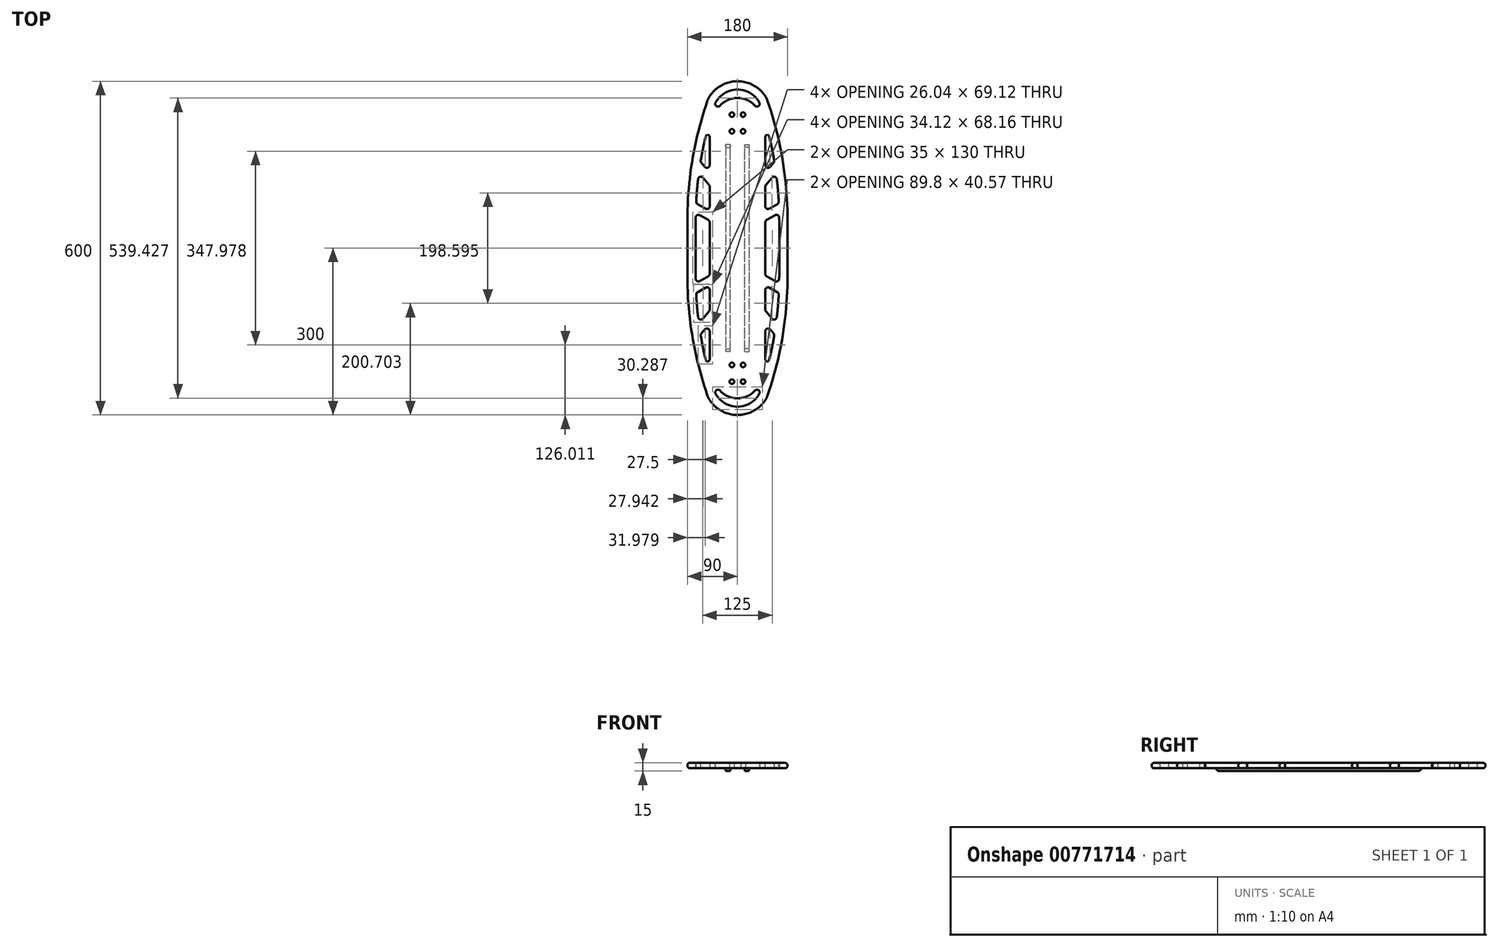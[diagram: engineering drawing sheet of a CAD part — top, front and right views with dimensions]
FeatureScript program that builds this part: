
annotation { "Feature Type Name" : "Feature", "Feature Type Description" : "" }
export const myFeature = defineFeature(function(context is Context, id is Id, definition is map)
    precondition{}
    {
        {
            var Q0;
            Q0=qCreatedBy(makeId("Top.planeOp"),FACE);
            var sketch = newSketch(context, id + "F0", { "sketchPlane" : qUnion([Q0])});
            skLineSegment(sketch, "E0", {"start": v(0, 0) * mm, "end": v(0, 270) * mm});
            skLineSegment(sketch, "E1", {"start": v(0, 0) * mm, "end": v(-50, 0) * mm});
            skLineSegment(sketch, "E2", {"start": v(-90, 0) * mm, "end": v(-90, 50) * mm});
            skArc(sketch, "E3", {"start": v(-53.96, 265.12) * mm, "mid": v(-80.93, 159.06) * mm, "end": v(-90, 50) * mm});
            skPoint(sketch, "E3.first.point", {"position": v(-90, 50) * mm});
            skArc(sketch, "E4", {"start": v(0, 300) * mm, "mid": v(-28.24, 292.94) * mm, "end": v(-49.83, 273.42) * mm});
            skPoint(sketch, "E5.visualSharp", {"position": v(-52.75, 268.59) * mm});
            skArc(sketch, "E5.filletArc", {"start": v(-49.83, 273.42) * mm, "mid": v(-52.16, 269.4) * mm, "end": v(-53.96, 265.12) * mm});
            skLineSegment(sketch, "E6", {"start": v(-75, 0) * mm, "end": v(-75, 50) * mm});
            skLineSegment(sketch, "E7", {"start": v(-50, 200) * mm, "end": v(-50, 149.42) * mm});
            skLineSegment(sketch, "E8.trimOffspring", {"start": v(-75, 0) * mm, "end": v(-90, 0) * mm});
            skPoint(sketch, "E9.visualSharp", {"position": v(-50, 27.86) * mm});
            skArc(sketch, "E10", {"start": v(-57.11, 200.84) * mm, "mid": v(-61.92, 179.23) * mm, "end": v(-65.98, 157.47) * mm});
            skArc(sketch, "E11", {"start": v(-50, 200) * mm, "mid": v(-53.18, 203.58) * mm, "end": v(-57.11, 200.84) * mm});
            skPoint(sketch, "E11.first.point", {"position": v(-57.11, 200.84) * mm});
            skPoint(sketch, "E11.second.point", {"position": v(-50, 200) * mm});
            skCircle(sketch, "E12", {"center": v(-10, 240) * mm, "radius": 4.1 * mm});
            skCircle(sketch, "E13", {"center": v(-10, 210) * mm, "radius": 4.1 * mm});
            skLineSegment(sketch, "E14", {"start": v(-10, 240) * mm, "end": v(-10, 210) * mm, "construction": true});
            skLineSegment(sketch, "E15.trimOffspring", {"start": v(0, 285) * mm, "end": v(0, 300) * mm});
            skArc(sketch, "E16", {"start": v(0, 285) * mm, "mid": v(-22.85, 278.76) * mm, "end": v(-39.38, 261.79) * mm});
            skLineSegment(sketch, "E17", {"start": v(-67.48, 59.33) * mm, "end": v(-52.5, 50.68) * mm});
            skLineSegment(sketch, "E18", {"start": v(-71.63, 79.05) * mm, "end": v(-57.5, 70.89) * mm});
            skArc(sketch, "E19.trimOffspring", {"start": v(-74.98, 55.04) * mm, "mid": v(-75, 52.52) * mm, "end": v(-75, 50) * mm});
            skLineSegment(sketch, "E20.trimOffspring", {"start": v(-50, 46.35) * mm, "end": v(-50, 0) * mm});
            skPoint(sketch, "E21.visualSharp", {"position": v(-74.27, 80.57) * mm});
            skArc(sketch, "E21.filletArc", {"start": v(-74.12, 83.64) * mm, "mid": v(-73.52, 80.99) * mm, "end": v(-71.63, 79.05) * mm});
            skPoint(sketch, "E22.visualSharp", {"position": v(-50, 66.56) * mm});
            skArc(sketch, "E22.filletArc", {"start": v(-57.5, 70.89) * mm, "mid": v(-52.5, 70.89) * mm, "end": v(-50, 75.22) * mm});
            skPoint(sketch, "E23.visualSharp", {"position": v(-50, 49.24) * mm});
            skArc(sketch, "E23.filletArc", {"start": v(-50, 46.35) * mm, "mid": v(-50.67, 48.85) * mm, "end": v(-52.5, 50.68) * mm});
            skPoint(sketch, "E24.visualSharp", {"position": v(-74.86, 63.59) * mm});
            skArc(sketch, "E24.filletArc", {"start": v(-67.48, 59.33) * mm, "mid": v(-72.46, 59.34) * mm, "end": v(-74.98, 55.04) * mm});
            skLineSegment(sketch, "E25", {"start": v(-64.88, 153.42) * mm, "end": v(-58.83, 146.2) * mm});
            skLineSegment(sketch, "E26", {"start": v(-51.17, 113.74) * mm, "end": v(-61.95, 126.59) * mm});
            skArc(sketch, "E27.trimOffspring", {"start": v(-70.75, 123.95) * mm, "mid": v(-72.75, 103.82) * mm, "end": v(-74.12, 83.64) * mm});
            skLineSegment(sketch, "E28.trimOffspring", {"start": v(-50, 110.53) * mm, "end": v(-50, 75.22) * mm});
            skPoint(sketch, "E29.visualSharp", {"position": v(-66.37, 155.19) * mm});
            skArc(sketch, "E29.filletArc", {"start": v(-65.98, 157.47) * mm, "mid": v(-65.88, 155.33) * mm, "end": v(-64.88, 153.42) * mm});
            skPoint(sketch, "E30.visualSharp", {"position": v(-50, 135.68) * mm});
            skArc(sketch, "E30.filletArc", {"start": v(-58.83, 146.2) * mm, "mid": v(-53.29, 144.72) * mm, "end": v(-50, 149.42) * mm});
            skPoint(sketch, "E31.visualSharp", {"position": v(-50, 112.35) * mm});
            skArc(sketch, "E31.filletArc", {"start": v(-50, 110.53) * mm, "mid": v(-50.3, 112.24) * mm, "end": v(-51.17, 113.74) * mm});
            skPoint(sketch, "E32.visualSharp", {"position": v(-69.32, 135.38) * mm});
            skArc(sketch, "E32.filletArc", {"start": v(-61.95, 126.59) * mm, "mid": v(-67.22, 128.16) * mm, "end": v(-70.75, 123.95) * mm});
            skArc(sketch, "E33", {"start": v(0, 270) * mm, "mid": v(-17.13, 266.35) * mm, "end": v(-31.28, 256.03) * mm});
            skArc(sketch, "E34.filletArc", {"start": v(-39.38, 261.79) * mm, "mid": v(-37.9, 255.29) * mm, "end": v(-31.28, 256.03) * mm});
            skSolve(sketch);
        }
        {
            var Q0;
            Q0=makeQuery(id+"F0.imprint","IMPRINT",FACE,{"disambiguationData":[TD([[makeQuery(id+"F0.imprint","IMPRINT",EDGE,{"derivedFrom":sQuery(id+"F0.wireOp",EDGE,"E0")}),1.0]])]});
            extrude(context, id + "F1", {"entities" : qUnion([Q0]), "depth" : 10 * mm, "offsetDistance" : 25 * mm});
        }
        {
            var Q0;
            Q0=makeQuery(id+"F1.opExtrude","CAP_EDGE",EDGE,{"disambiguationData":[OSD([sQuery(id+"F0.wireOp",EDGE,"E2")])],"isStart":false});
            var Q1;
            Q1=makeQuery(id+"F1.opExtrude","CAP_EDGE",EDGE,{"disambiguationData":[OSD([sQuery(id+"F0.wireOp",EDGE,"E2")])],"isStart":true});
            fillet(context, id + "F2", {"entities" : qUnion([Q0, Q1]), "radius" : 5 * mm, "tangentPropagation" : true, "allowEdgeOverflow" : false});
        }
        {
            var Q0;
            {var subQ0=makeQuery(id+"F1.opExtrude","CAP_FACE",FACE,{"disambiguationData":[OSD([sQuery(id+"F0.wireOp",EDGE,"E0"),sQuery(id+"F0.wireOp",EDGE,"E1"),sQuery(id+"F0.wireOp",EDGE,"E2"),sQuery(id+"F0.wireOp",EDGE,"E3"),sQuery(id+"F0.wireOp",EDGE,"E4"),sQuery(id+"F0.wireOp",EDGE,"E5.filletArc"),sQuery(id+"F0.wireOp",EDGE,"E6"),sQuery(id+"F0.wireOp",EDGE,"E7"),sQuery(id+"F0.wireOp",EDGE,"E8.trimOffspring"),sQuery(id+"F0.wireOp",EDGE,"E10"),sQuery(id+"F0.wireOp",EDGE,"E11"),sQuery(id+"F0.wireOp",EDGE,"E12"),sQuery(id+"F0.wireOp",EDGE,"E13"),sQuery(id+"F0.wireOp",EDGE,"E15.trimOffspring"),sQuery(id+"F0.wireOp",EDGE,"E16"),sQuery(id+"F0.wireOp",EDGE,"w8QJj0XE-BuEV-9lwG-eJEp-A0GvQwhFIuGf"),sQuery(id+"F0.wireOp",EDGE,"Jj9zvzCL-fS3g-TJDC-V5ka-80Cxc9p66nId"),sQuery(id+"F0.wireOp",EDGE,"E17"),sQuery(id+"F0.wireOp",EDGE,"E18"),sQuery(id+"F0.wireOp",EDGE,"E19.trimOffspring"),sQuery(id+"F0.wireOp",EDGE,"E20.trimOffspring"),sQuery(id+"F0.wireOp",EDGE,"E21.filletArc"),sQuery(id+"F0.wireOp",EDGE,"E22.filletArc"),sQuery(id+"F0.wireOp",EDGE,"E23.filletArc"),sQuery(id+"F0.wireOp",EDGE,"E24.filletArc"),sQuery(id+"F0.wireOp",EDGE,"E25"),sQuery(id+"F0.wireOp",EDGE,"E26"),sQuery(id+"F0.wireOp",EDGE,"E27.trimOffspring"),sQuery(id+"F0.wireOp",EDGE,"E28.trimOffspring"),sQuery(id+"F0.wireOp",EDGE,"E29.filletArc"),sQuery(id+"F0.wireOp",EDGE,"E30.filletArc"),sQuery(id+"F0.wireOp",EDGE,"E31.filletArc"),sQuery(id+"F0.wireOp",EDGE,"E32.filletArc")])],"isStart":true});var subQ1=makeQuery(id+"F7.boolean.opBoolean","MERGE",FACE,{"derivedFrom":[subQ0,makeQuery(id+"F7.opPattern","COPY",FACE,{"derivedFrom":subQ0,"instanceName":"1"})]});Q0=makeQuery(id+"F8.boolean.opBoolean","MERGE",FACE,{"derivedFrom":[subQ1,makeQuery(id+"F8.opPattern","COPY",FACE,{"derivedFrom":subQ1,"instanceName":"1"})]});}
            var sketch = newSketch(context, id + "F3", { "sketchPlane" : qUnion([Q0])});
            skLineSegment(sketch, "E35", {"start": v(-13, 0) * mm, "end": v(-13, -185.98) * mm});
            skLineSegment(sketch, "E36", {"start": v(-13, -185.98) * mm, "end": v(-20.93, -185.98) * mm});
            skLineSegment(sketch, "E37", {"start": v(-20.93, -185.98) * mm, "end": v(-20.93, 0) * mm});
            skLineSegment(sketch, "E38", {"start": v(-20.93, 0) * mm, "end": v(-13, 0) * mm});
            skSolve(sketch);
        }
        {
            var Q0;
            Q0=makeQuery(id+"F3.imprint","IMPRINT",FACE,{"disambiguationData":[TD([[makeQuery(id+"F3.imprint","IMPRINT",EDGE,{"derivedFrom":sQuery(id+"F3.wireOp",EDGE,"E35")}),-1.0]])]});
            extrude(context, id + "F4", {"entities" : qUnion([Q0]), "operationType" : NewBodyOperationType.ADD, "depth" : 5 * mm, "offsetDistance" : 25 * mm});
        }
        {
            var Q0;
            Q0=makeQuery(id+"F4.opExtrude","CAP_EDGE",EDGE,{"disambiguationData":[OSD([sQuery(id+"F3.wireOp",EDGE,"E36")])],"isStart":false});
            chamfer(context, id + "F5", {"entities" : qUnion([Q0]), "width" : 5 * mm, "tangentPropagation" : true});
        }
        {
            var Q0;
            Q0=makeQuery(id+"F1.opExtrude","SWEPT_FACE",FACE,{"disambiguationData":[OSD([sQuery(id+"F0.wireOp",EDGE,"E27.trimOffspring")])]});
            var Q1;
            Q1=makeQuery(id+"F1.opExtrude","SWEPT_FACE",FACE,{"disambiguationData":[OSD([sQuery(id+"F0.wireOp",EDGE,"E19.trimOffspring")])]});
            var Q2;
            Q2=makeQuery(id+"F1.opExtrude","SWEPT_FACE",FACE,{"disambiguationData":[OSD([sQuery(id+"F0.wireOp",EDGE,"E10")])]});
            var Q3;
            Q3=makeQuery(id+"F1.opExtrude","SWEPT_FACE",FACE,{"disambiguationData":[OSD([sQuery(id+"F0.wireOp",EDGE,"Jj9zvzCL-fS3g-TJDC-V5ka-80Cxc9p66nId")])]});
            var Q4;
            Q4=makeQuery(id+"F1.opExtrude","SWEPT_FACE",FACE,{"disambiguationData":[OSD([sQuery(id+"F0.wireOp",EDGE,"E34.filletArc")])]});
            fillet(context, id + "F6", {"entities" : qUnion([Q0, Q1, Q2, Q3, Q4]), "radius" : 5 * mm, "tangentPropagation" : true, "allowEdgeOverflow" : false});
        }
        {
            var Q0;
            Q0=makeQuery(id+"F1.opExtrude","SWEPT_BODY",BODY,{"disambiguationData":[OSD([sQuery(id+"F0.wireOp",EDGE,"E0"),sQuery(id+"F0.wireOp",EDGE,"E1"),sQuery(id+"F0.wireOp",EDGE,"E2"),sQuery(id+"F0.wireOp",EDGE,"E3"),sQuery(id+"F0.wireOp",EDGE,"E4"),sQuery(id+"F0.wireOp",EDGE,"70fVyuo6-xFZn-wcj5-HDp9-3M0uHGLZeAUQ"),sQuery(id+"F0.wireOp",EDGE,"E5.filletArc")])]});
            var Q1;
            Q1=qCreatedBy(makeId("Right.planeOp"),FACE);
            mirror(context, id + "F7", {"operationType" : NewBodyOperationType.ADD, "entities" : qUnion([Q0]), "mirrorPlane" : qUnion([Q1])});
        }
        {
            var Q0;
            Q0=makeQuery(id+"F1.opExtrude","SWEPT_BODY",BODY,{"disambiguationData":[OSD([sQuery(id+"F0.wireOp",EDGE,"E0"),sQuery(id+"F0.wireOp",EDGE,"E1"),sQuery(id+"F0.wireOp",EDGE,"E2"),sQuery(id+"F0.wireOp",EDGE,"E3"),sQuery(id+"F0.wireOp",EDGE,"E4"),sQuery(id+"F0.wireOp",EDGE,"70fVyuo6-xFZn-wcj5-HDp9-3M0uHGLZeAUQ"),sQuery(id+"F0.wireOp",EDGE,"E5.filletArc")])]});
            var Q1;
            Q1=qCreatedBy(makeId("Front.planeOp"),FACE);
            mirror(context, id + "F8", {"operationType" : NewBodyOperationType.ADD, "entities" : qUnion([Q0]), "mirrorPlane" : qUnion([Q1])});
        }
    });
